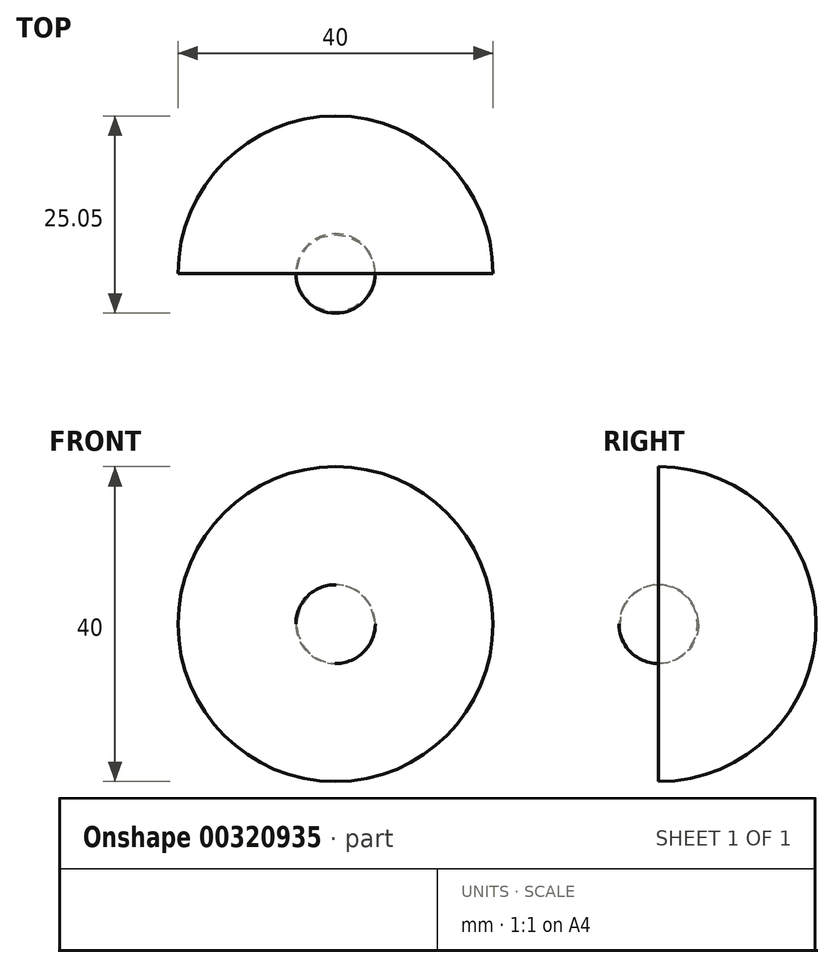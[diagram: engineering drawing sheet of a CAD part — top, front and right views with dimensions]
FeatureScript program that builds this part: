
annotation { "Feature Type Name" : "Feature", "Feature Type Description" : "" }
export const myFeature = defineFeature(function(context is Context, id is Id, definition is map)
    precondition{}
    {
        {
            var Q0;
            Q0=qCreatedBy(makeId("Front.planeOp"),FACE);
            var sketch = newSketch(context, id + "F0", { "sketchPlane" : qUnion([Q0])});
            skLineSegment(sketch, "E0", {"start": v(0, 0) * mm, "end": v(0, 40) * mm});
            skArc(sketch, "E1", {"start": v(0, 0) * mm, "mid": v(20, 20) * mm, "end": v(0, 40) * mm});
            skSolve(sketch);
        }
        {
            var Q0;
            Q0=makeQuery(id+"F0.imprint","IMPRINT",FACE,{"disambiguationData":[TD([[makeQuery(id+"F0.imprint","IMPRINT",EDGE,{"derivedFrom":sQuery(id+"F0.wireOp",EDGE,"E0")}),-1.0]])]});
            var Q1;
            Q1=sQuery(id+"F0.wireOp",EDGE,"E0");
            revolve(context, id + "F1", {"entities" : qUnion([Q0]), "axis" : qUnion([Q1]), "revolveType" : RevolveType.ONE_DIRECTION, "angle" : 180 * degree});
        }
        {
            var Q0;
            Q0=makeQuery(id+"F1.opRevolve","CAP_FACE",FACE,{"disambiguationData":[OSD([sQuery(id+"F0.wireOp",EDGE,"E0"),sQuery(id+"F0.wireOp",EDGE,"E1")])],"isStart":true});
            var sketch = newSketch(context, id + "F2", { "sketchPlane" : qUnion([Q0])});
            skPoint(sketch, "E2", {"position": v(0, 15) * mm});
            skArc(sketch, "E3", {"start": v(0, 15) * mm, "mid": v(5.05, 20) * mm, "end": v(0, 25) * mm});
            skLineSegment(sketch, "E4", {"start": v(0, 15) * mm, "end": v(0, 25) * mm});
            skSolve(sketch);
        }
        {
            var Q0;
            Q0 = qSketchRegion(id + "F2", true);
            var Q1;
            Q1=sQuery(id+"F2.wireOp",EDGE,"E4");
            revolve(context, id + "F3", {"entities" : qUnion([Q0]), "axis" : qUnion([Q1]), "revolveType" : RevolveType.FULL});
        }
    });
